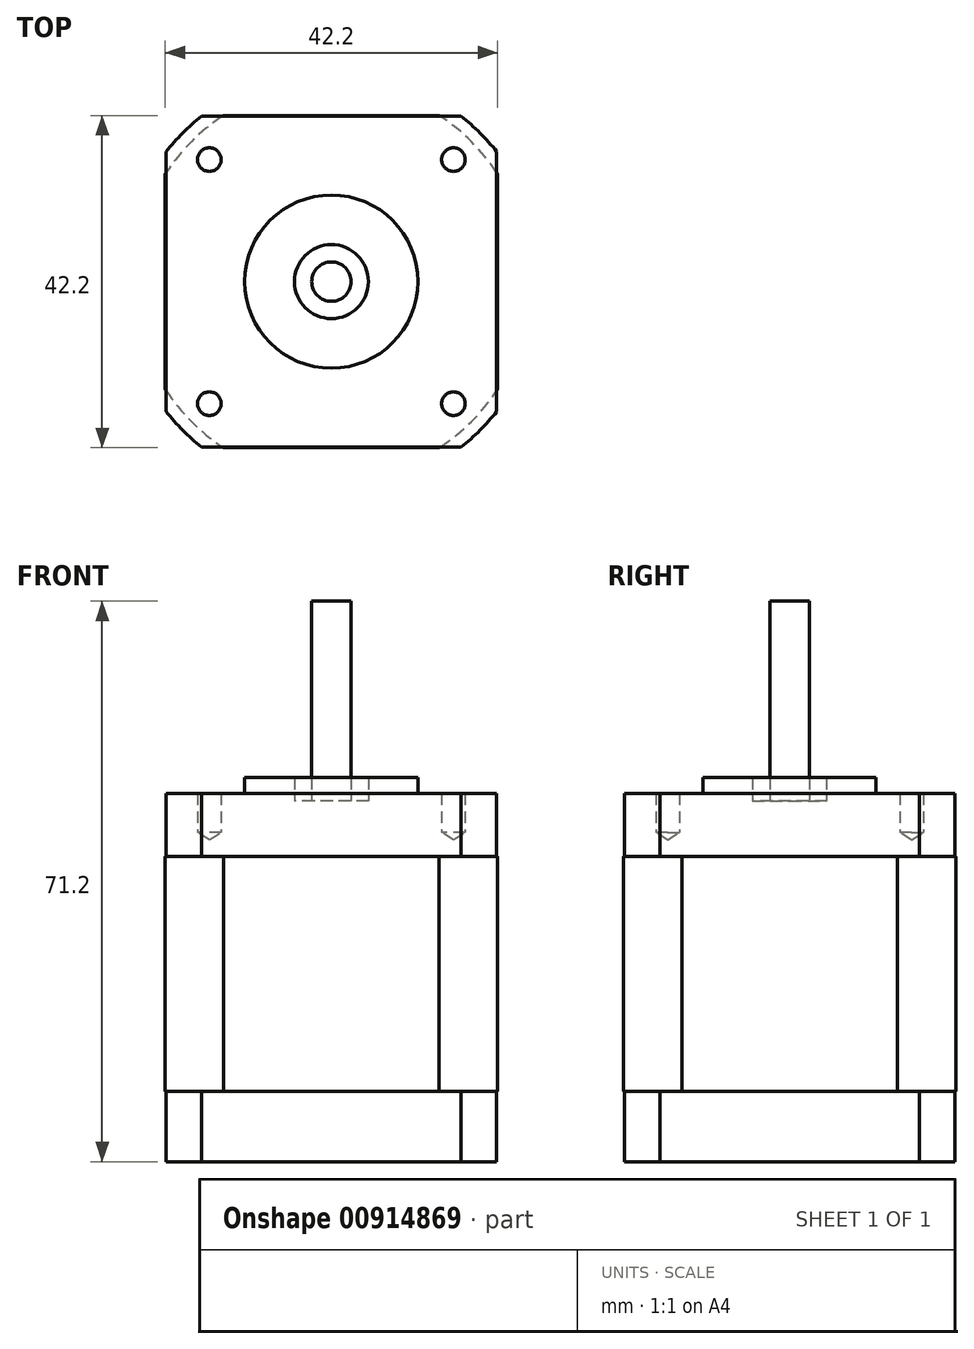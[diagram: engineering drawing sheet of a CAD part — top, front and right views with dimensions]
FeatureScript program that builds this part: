
annotation { "Feature Type Name" : "Feature", "Feature Type Description" : "" }
export const myFeature = defineFeature(function(context is Context, id is Id, definition is map)
    precondition{}
    {
        {
            assignVariable(context, id + "F0", {"name" : "BodyL", "anyValue" : 29.9});
        }
        {
            var Q0;
            Q0=qCreatedBy(makeId("Top.planeOp"),FACE);
            var sketch = newSketch(context, id + "F1", { "sketchPlane" : qUnion([Q0])});
            skLineSegment(sketch, "E0.bottom", {"start": v(21, 21) * mm, "end": v(16.49, 21) * mm, "construction": true});
            skLineSegment(sketch, "E0.top", {"start": v(21, -21) * mm, "end": v(16.49, -21) * mm, "construction": true});
            skLineSegment(sketch, "E0.left", {"start": v(21, 21) * mm, "end": v(21, 16.49) * mm, "construction": true});
            skLineSegment(sketch, "E0.right", {"start": v(-21, 21) * mm, "end": v(-21, 16.49) * mm, "construction": true});
            skPoint(sketch, "E0.middle", {"position": v(0, 0) * mm});
            skLineSegment(sketch, "E1", {"start": v(16.49, 21) * mm, "end": v(-16.49, 21) * mm});
            skLineSegment(sketch, "E2", {"start": v(21, 16.49) * mm, "end": v(21, -16.49) * mm});
            skArc(sketch, "E3", {"start": v(21, 16.49) * mm, "mid": v(18.88, 18.88) * mm, "end": v(16.49, 21) * mm});
            skArc(sketch, "E4", {"start": v(16.49, 21) * mm, "mid": v(0, 26.7) * mm, "end": v(-16.49, 21) * mm, "construction": true});
            skLineSegment(sketch, "E5", {"start": v(-16.49, 21) * mm, "end": v(-21, 21) * mm, "construction": true});
            skArc(sketch, "E6", {"start": v(-16.49, 21) * mm, "mid": v(-18.88, 18.88) * mm, "end": v(-21, 16.49) * mm});
            skLineSegment(sketch, "E7", {"start": v(-21, 16.49) * mm, "end": v(-21, -16.49) * mm});
            skArc(sketch, "E8", {"start": v(-21, 16.49) * mm, "mid": v(-26.7, 0) * mm, "end": v(-21, -16.49) * mm, "construction": true});
            skArc(sketch, "E9", {"start": v(-21, -16.49) * mm, "mid": v(-18.88, -18.88) * mm, "end": v(-16.49, -21) * mm});
            skLineSegment(sketch, "E10", {"start": v(-21, -16.49) * mm, "end": v(-21, -21) * mm, "construction": true});
            skLineSegment(sketch, "E11", {"start": v(-16.49, -21) * mm, "end": v(-21, -21) * mm, "construction": true});
            skArc(sketch, "E12", {"start": v(-16.49, -21) * mm, "mid": v(0, -26.7) * mm, "end": v(16.49, -21) * mm, "construction": true});
            skLineSegment(sketch, "E13", {"start": v(16.49, -21) * mm, "end": v(-16.49, -21) * mm});
            skArc(sketch, "E14", {"start": v(16.49, -21) * mm, "mid": v(18.88, -18.88) * mm, "end": v(21, -16.49) * mm});
            skLineSegment(sketch, "E15", {"start": v(21, -16.49) * mm, "end": v(21, -21) * mm, "construction": true});
            skArc(sketch, "E16", {"start": v(21, -16.49) * mm, "mid": v(26.7, 0) * mm, "end": v(21, 16.49) * mm, "construction": true});
            skSolve(sketch);
        }
        {
            var Q0;
            Q0=qCreatedBy(makeId("Top.planeOp"),FACE);
            cPlane(context, id + "F2", {"entities" : qUnion([Q0]), "cplaneType" : CPlaneType.OFFSET, "offset" : 8 * mm, "oppositeDirection" : true, "width" : 150 * mm, "height" : 150 * mm});
        }
        {
            var Q0;
            Q0=makeQuery(id+"F1.imprint","IMPRINT",FACE,{"disambiguationData":[TD([[makeQuery(id+"F1.imprint","IMPRINT",EDGE,{"derivedFrom":sQuery(id+"F1.wireOp",EDGE,"E1")}),1.0]])]});
            var Q1;
            Q1=qCreatedBy(id+"F2.planeOp",FACE);
            extrude(context, id + "F3", {"entities" : qUnion([Q0]), "endBound" : BoundingType.UP_TO_SURFACE, "oppositeDirection" : true, "depth" : 25 * mm, "endBoundEntityFace" : qUnion([Q1]), "offsetDistance" : 25 * mm});
        }
        {
            var Q0;
            Q0=qCreatedBy(id+"F2.planeOp",FACE);
            cPlane(context, id + "F4", {"entities" : qUnion([Q0]), "cplaneType" : CPlaneType.OFFSET, "offset" : (getVariable(context, 'BodyL')) * mm, "oppositeDirection" : true, "width" : 150 * mm, "height" : 150 * mm});
        }
        {
            var Q0;
            Q0=qCreatedBy(id+"F4.planeOp",FACE);
            var sketch = newSketch(context, id + "F5", { "sketchPlane" : qUnion([Q0])});
            skLineSegment(sketch, "E17.bottom", {"start": v(-13.69, -21.1) * mm, "end": v(13.69, -21.1) * mm});
            skLineSegment(sketch, "E17.top", {"start": v(-13.69, 21.1) * mm, "end": v(13.69, 21.1) * mm});
            skLineSegment(sketch, "E17.left", {"start": v(-21.1, -13.69) * mm, "end": v(-21.1, 13.69) * mm});
            skLineSegment(sketch, "E17.right", {"start": v(21.1, -13.69) * mm, "end": v(21.1, 13.69) * mm});
            skPoint(sketch, "E17.middle", {"position": v(0, 0) * mm});
            skArc(sketch, "E18", {"start": v(13.69, -21.1) * mm, "mid": v(17.78, -17.78) * mm, "end": v(21.1, -13.69) * mm});
            skPoint(sketch, "E19.orphan", {"position": v(-21.1, -21.1) * mm});
            skPoint(sketch, "E20.orphan", {"position": v(21.1, -21.1) * mm});
            skArc(sketch, "E21.trimOffspring", {"start": v(21.1, 13.69) * mm, "mid": v(17.78, 17.78) * mm, "end": v(13.69, 21.1) * mm});
            skPoint(sketch, "E22.orphan", {"position": v(21.1, 21.1) * mm});
            skArc(sketch, "E23.trimOffspring", {"start": v(-13.69, 21.1) * mm, "mid": v(-17.78, 17.78) * mm, "end": v(-21.1, 13.69) * mm});
            skPoint(sketch, "E24.orphan", {"position": v(-21.1, 21.1) * mm});
            skArc(sketch, "E25.trimOffspring", {"start": v(-21.1, -13.69) * mm, "mid": v(-17.78, -17.78) * mm, "end": v(-13.69, -21.1) * mm});
            skSolve(sketch);
        }
        {
            var Q0;
            Q0=makeQuery(id+"F5.imprint","IMPRINT",FACE,{"disambiguationData":[TD([[makeQuery(id+"F5.imprint","IMPRINT",EDGE,{"derivedFrom":sQuery(id+"F5.wireOp",EDGE,"E17.bottom")}),1.0]])]});
            var Q1;
            Q1=qCreatedBy(id+"F2.planeOp",FACE);
            extrude(context, id + "F6", {"entities" : qUnion([Q0]), "operationType" : NewBodyOperationType.ADD, "endBound" : BoundingType.UP_TO_SURFACE, "depth" : 25 * mm, "endBoundEntityFace" : qUnion([Q1]), "offsetDistance" : 25 * mm});
        }
        {
            var Q0;
            Q0=qCreatedBy(id+"F4.planeOp",FACE);
            var sketch = newSketch(context, id + "F7", { "sketchPlane" : qUnion([Q0])});
            skLineSegment(sketch, "E26.0", {"start": v(16.49, 21) * mm, "end": v(-16.49, 21) * mm});
            skArc(sketch, "E27.0", {"start": v(-16.49, 21) * mm, "mid": v(-18.88, 18.88) * mm, "end": v(-21, 16.49) * mm});
            skLineSegment(sketch, "E28.0", {"start": v(-21, 16.49) * mm, "end": v(-21, -16.49) * mm});
            skArc(sketch, "E29.0", {"start": v(-21, -16.49) * mm, "mid": v(-18.88, -18.88) * mm, "end": v(-16.49, -21) * mm});
            skLineSegment(sketch, "E30.0", {"start": v(16.49, -21) * mm, "end": v(-16.49, -21) * mm});
            skArc(sketch, "E31.0", {"start": v(16.49, -21) * mm, "mid": v(18.88, -18.88) * mm, "end": v(21, -16.49) * mm});
            skLineSegment(sketch, "E32.0", {"start": v(21, 16.49) * mm, "end": v(21, -16.49) * mm});
            skArc(sketch, "E33.0", {"start": v(21, 16.49) * mm, "mid": v(18.88, 18.88) * mm, "end": v(16.49, 21) * mm});
            skSolve(sketch);
        }
        {
            var Q0;
            Q0 = qSketchRegion(id + "F7", true);
            extrude(context, id + "F8", {"entities" : qUnion([Q0]), "operationType" : NewBodyOperationType.ADD, "oppositeDirection" : true, "depth" : 8.9 * mm, "offsetDistance" : 25 * mm});
        }
        {
            var Q0;
            Q0=qCreatedBy(makeId("Top.planeOp"),FACE);
            var sketch = newSketch(context, id + "F9", { "sketchPlane" : qUnion([Q0])});
            skPoint(sketch, "E34.0", {"position": v(0, 0) * mm});
            skCircle(sketch, "E35", {"center": v(0, 0) * mm, "radius": 11 * mm});
            skCircle(sketch, "E36", {"center": v(0, 0) * mm, "radius": 4.7 * mm});
            skSolve(sketch);
        }
        {
            var Q0;
            Q0=makeQuery(id+"F9.imprint","IMPRINT",FACE,{"disambiguationData":[TD([[makeQuery(id+"F9.imprint","IMPRINT",EDGE,{"derivedFrom":sQuery(id+"F9.wireOp",EDGE,"E35")}),1.0]])]});
            extrude(context, id + "F10", {"entities" : qUnion([Q0]), "operationType" : NewBodyOperationType.ADD, "depth" : 2 * mm, "offsetDistance" : 25 * mm});
        }
        {
            var Q0;
            Q0=makeQuery(id+"F10.opExtrude","CAP_FACE",FACE,{"disambiguationData":[OSD([sQuery(id+"F9.wireOp",EDGE,"E35"),sQuery(id+"F9.wireOp",EDGE,"E36")])],"isStart":false});
            var sketch = newSketch(context, id + "F11", { "sketchPlane" : qUnion([Q0])});
            skCircle(sketch, "E37", {"center": v(0, 0) * mm, "radius": 2.5 * mm});
            skCircle(sketch, "E38.0", {"center": v(0, 0) * mm, "radius": 4.7 * mm});
            skSolve(sketch);
        }
        {
            var Q0;
            Q0=makeQuery(id+"F11.imprint","IMPRINT",FACE,{"disambiguationData":[TD([[makeQuery(id+"F11.imprint","IMPRINT",EDGE,{"derivedFrom":sQuery(id+"F11.wireOp",EDGE,"E37")}),1.0]])]});
            extrude(context, id + "F12", {"entities" : qUnion([Q0]), "operationType" : NewBodyOperationType.ADD, "depth" : 22.4 * mm, "offsetDistance" : 25 * mm, "hasSecondDirection" : true, "secondDirectionOppositeDirection" : true, "secondDirectionDepth" : 10 * mm});
        }
        {
            var Q0;
            Q0=makeQuery(id+"F11.imprint","IMPRINT",FACE,{"disambiguationData":[TD([[makeQuery(id+"F11.imprint","IMPRINT",EDGE,{"derivedFrom":sQuery(id+"F11.wireOp",EDGE,"E37")}),-1.0]])]});
            extrude(context, id + "F13", {"entities" : qUnion([Q0]), "operationType" : NewBodyOperationType.REMOVE, "oppositeDirection" : true, "depth" : 3 * mm, "offsetDistance" : 25 * mm});
        }
        {
            var Q0;
            Q0=qCreatedBy(makeId("Top.planeOp"),FACE);
            var sketch = newSketch(context, id + "F14", { "sketchPlane" : qUnion([Q0])});
            skPoint(sketch, "E39.0", {"position": v(0, 0) * mm});
            skLineSegment(sketch, "E40.bottom", {"start": v(15.5, 15.5) * mm, "end": v(-15.5, 15.5) * mm, "construction": true});
            skLineSegment(sketch, "E40.top", {"start": v(15.5, -15.5) * mm, "end": v(-15.5, -15.5) * mm, "construction": true});
            skLineSegment(sketch, "E40.left", {"start": v(15.5, 15.5) * mm, "end": v(15.5, -15.5) * mm, "construction": true});
            skLineSegment(sketch, "E40.right", {"start": v(-15.5, 15.5) * mm, "end": v(-15.5, -15.5) * mm, "construction": true});
            skSolve(sketch);
        }
        {
            var Q0;
            Q0=sQuery(id+"F14.wireOp",VERTEX,"E40.bottom.end");
            var Q1;
            Q1=sQuery(id+"F14.wireOp",VERTEX,"E40.bottom.start");
            var Q2;
            Q2=sQuery(id+"F14.wireOp",VERTEX,"E40.top.start");
            var Q3;
            Q3=sQuery(id+"F14.wireOp",VERTEX,"E40.top.end");
            var Q4;
            Q4=makeQuery(id+"F3.opExtrude","SWEPT_BODY",BODY,{"disambiguationData":[OSD([sQuery(id+"F1.wireOp",EDGE,"E1"),sQuery(id+"F1.wireOp",EDGE,"E2"),sQuery(id+"F1.wireOp",EDGE,"E3"),sQuery(id+"F1.wireOp",EDGE,"E6"),sQuery(id+"F1.wireOp",EDGE,"E7"),sQuery(id+"F1.wireOp",EDGE,"E9"),sQuery(id+"F1.wireOp",EDGE,"E13"),sQuery(id+"F1.wireOp",EDGE,"E14")])]});
            hole(context, id + "F15", {"style" : HoleStyle.SIMPLE, "endStyle" : HoleEndStyle.BLIND, "holeDiameter" : 3 * mm, "majorDiameter" : 5 * mm, "holeDepth" : 5 * mm, "isTappedThrough" : true, "tappedDepth" : 12 * mm, "tapClearance" : 3, "locations" : qUnion([Q0, Q1, Q2, Q3]), "scope" : qUnion([Q4]), "startStyle" : HoleStartStyle.PART});
        }
    });
